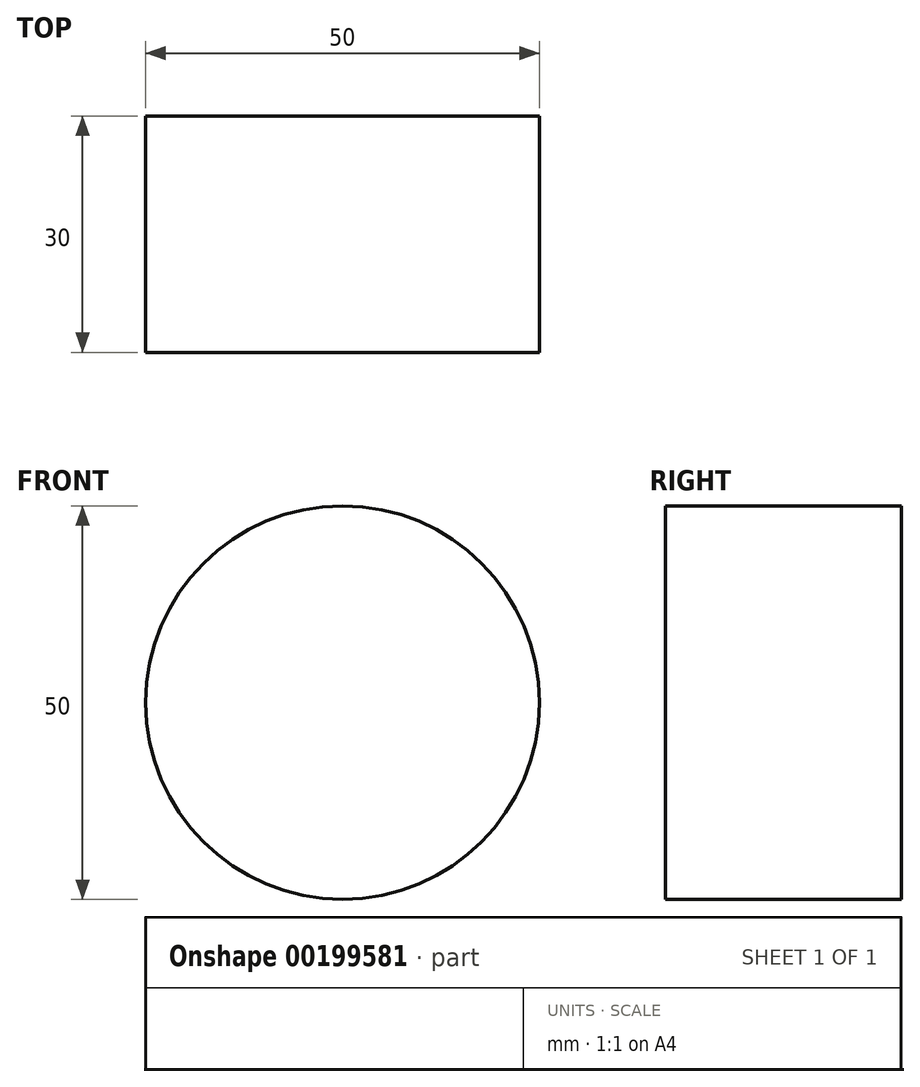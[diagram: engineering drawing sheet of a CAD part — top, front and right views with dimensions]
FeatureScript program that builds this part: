
annotation { "Feature Type Name" : "Feature", "Feature Type Description" : "" }
export const myFeature = defineFeature(function(context is Context, id is Id, definition is map)
    precondition{}
    {
        {
            var Q0;
            Q0=qCreatedBy(makeId("Front.planeOp"),FACE);
            var sketch = newSketch(context, id + "F0", { "sketchPlane" : qUnion([Q0])});
            skCircle(sketch, "E0", {"center": v(0, 0) * mm, "radius": 25 * mm});
            skSolve(sketch);
        }
        {
            var Q0;
            Q0=makeQuery(id+"F0.imprint","IMPRINT",FACE,{"disambiguationData":[TD([[makeQuery(id+"F0.imprint","IMPRINT",EDGE,{"derivedFrom":sQuery(id+"F0.wireOp",EDGE,"E0")}),1.0]])]});
            extrude(context, id + "F1", {"entities" : qUnion([Q0]), "endBound" : BoundingType.SYMMETRIC, "depth" : 30 * mm});
        }
    });
